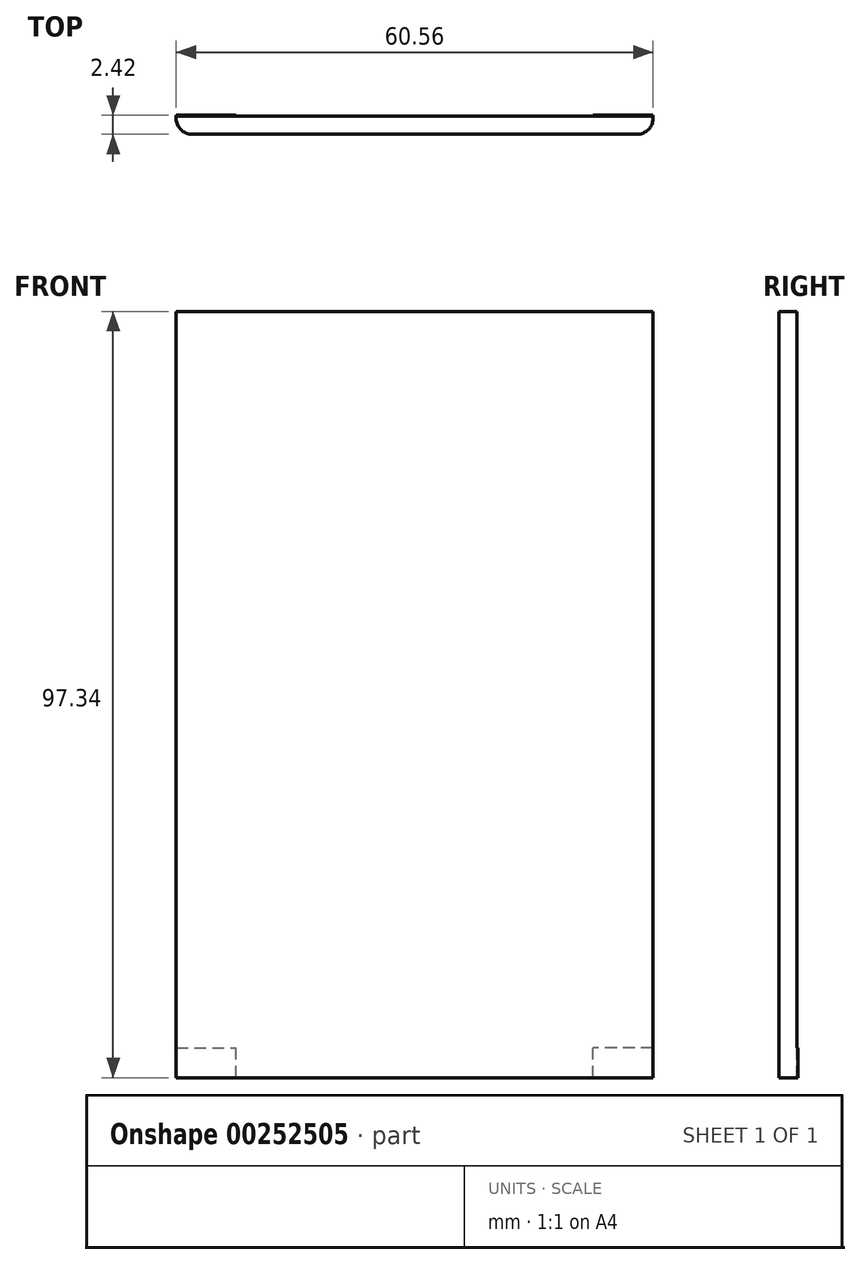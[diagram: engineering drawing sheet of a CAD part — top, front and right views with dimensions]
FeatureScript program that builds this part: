
annotation { "Feature Type Name" : "Feature", "Feature Type Description" : "" }
export const myFeature = defineFeature(function(context is Context, id is Id, definition is map)
    precondition{}
    {
        {
            var Q0;
            Q0=qCreatedBy(makeId("Front.planeOp"),FACE);
            var sketch = newSketch(context, id + "F0", { "sketchPlane" : qUnion([Q0])});
            skLineSegment(sketch, "E0.bottom", {"start": v(-30.28, -48.67) * mm, "end": v(30.28, -48.67) * mm});
            skLineSegment(sketch, "E0.top", {"start": v(-30.28, 48.67) * mm, "end": v(30.28, 48.67) * mm});
            skLineSegment(sketch, "E0.left", {"start": v(-30.28, -48.67) * mm, "end": v(-30.28, 48.67) * mm});
            skLineSegment(sketch, "E0.right", {"start": v(30.28, -48.67) * mm, "end": v(30.28, 48.67) * mm});
            skPoint(sketch, "E0.middle", {"position": v(0, 0) * mm});
            skSolve(sketch);
        }
        {
            var Q0;
            Q0=makeQuery(id+"F0.imprint","IMPRINT",FACE,{"disambiguationData":[TD([[makeQuery(id+"F0.imprint","IMPRINT",EDGE,{"derivedFrom":sQuery(id+"F0.wireOp",EDGE,"E0.bottom")}),1.0]])]});
            extrude(context, id + "F1", {"entities" : qUnion([Q0]), "depth" : 2.3 * mm});
        }
        {
            var Q0;
            Q0=makeQuery(id+"F1.opExtrude","CAP_EDGE",EDGE,{"disambiguationData":[OSD([sQuery(id+"F0.wireOp",EDGE,"E0.right")])],"isStart":false});
            var Q1;
            Q1=makeQuery(id+"F1.opExtrude","CAP_EDGE",EDGE,{"disambiguationData":[OSD([sQuery(id+"F0.wireOp",EDGE,"E0.left")])],"isStart":false});
            fillet(context, id + "F2", {"entities" : qUnion([Q0, Q1]), "radius" : 2.03 * mm, "tangentPropagation" : true, "allowEdgeOverflow" : false});
        }
        {
            var Q0;
            Q0=makeQuery(id+"F1.opExtrude","CAP_FACE",FACE,{"disambiguationData":[OSD([sQuery(id+"F0.wireOp",EDGE,"E0.bottom"),sQuery(id+"F0.wireOp",EDGE,"E0.top"),sQuery(id+"F0.wireOp",EDGE,"E0.left"),sQuery(id+"F0.wireOp",EDGE,"E0.right")])],"isStart":true});
            var sketch = newSketch(context, id + "F3", { "sketchPlane" : qUnion([Q0])});
            skLineSegment(sketch, "E1.bottom", {"start": v(-30.28, -48.67) * mm, "end": v(-22.66, -48.67) * mm});
            skLineSegment(sketch, "E1.top", {"start": v(-30.28, -44.86) * mm, "end": v(-22.66, -44.86) * mm});
            skLineSegment(sketch, "E1.left", {"start": v(-30.28, -48.67) * mm, "end": v(-30.28, -44.86) * mm});
            skLineSegment(sketch, "E1.right", {"start": v(-22.66, -48.67) * mm, "end": v(-22.66, -44.86) * mm});
            skLineSegment(sketch, "E2.bottom", {"start": v(30.28, -48.67) * mm, "end": v(22.66, -48.67) * mm});
            skLineSegment(sketch, "E2.top", {"start": v(30.28, -44.86) * mm, "end": v(22.66, -44.86) * mm});
            skLineSegment(sketch, "E2.left", {"start": v(30.28, -48.67) * mm, "end": v(30.28, -44.86) * mm});
            skLineSegment(sketch, "E2.right", {"start": v(22.66, -48.67) * mm, "end": v(22.66, -44.86) * mm});
            skSolve(sketch);
        }
        {
            var Q0;
            Q0=makeQuery(id+"F3.imprint","IMPRINT",FACE,{"disambiguationData":[TD([[makeQuery(id+"F3.imprint","IMPRINT",EDGE,{"derivedFrom":sQuery(id+"F3.wireOp",EDGE,"E1.bottom")}),-1.0]])]});
            var Q1;
            Q1=makeQuery(id+"F3.imprint","IMPRINT",FACE,{"disambiguationData":[TD([[makeQuery(id+"F3.imprint","IMPRINT",EDGE,{"derivedFrom":sQuery(id+"F3.wireOp",EDGE,"E2.bottom")}),-1.0]])]});
            extrude(context, id + "F4", {"entities" : qUnion([Q0, Q1]), "operationType" : NewBodyOperationType.ADD, "endBound" : BoundingType.SYMMETRIC, "depth" : 0.25 * mm});
        }
    });
